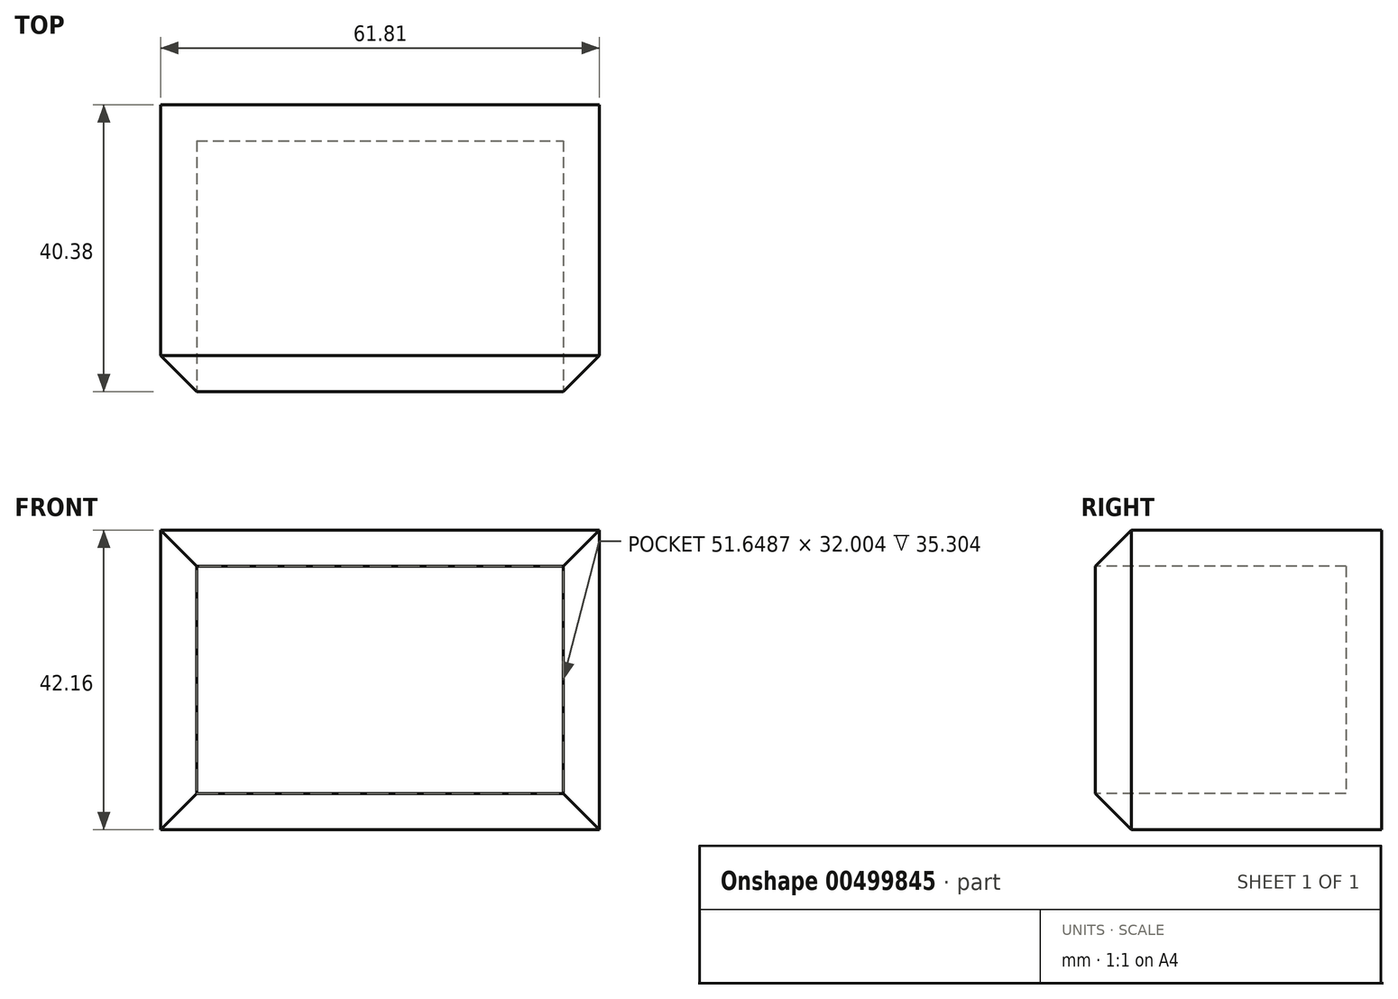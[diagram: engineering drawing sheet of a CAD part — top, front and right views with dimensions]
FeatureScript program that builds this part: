
annotation { "Feature Type Name" : "Feature", "Feature Type Description" : "" }
export const myFeature = defineFeature(function(context is Context, id is Id, definition is map)
    precondition{}
    {
        {
            var Q0;
            Q0=qCreatedBy(makeId("Top.planeOp"),FACE);
            var sketch = newSketch(context, id + "F0", { "sketchPlane" : qUnion([Q0])});
            skLineSegment(sketch, "E0.bottom", {"start": v(-33.75, 22.18) * mm, "end": v(28.06, 22.18) * mm});
            skLineSegment(sketch, "E0.top", {"start": v(-33.75, -18.2) * mm, "end": v(28.06, -18.2) * mm});
            skLineSegment(sketch, "E0.left", {"start": v(-33.75, 22.18) * mm, "end": v(-33.75, -18.2) * mm});
            skLineSegment(sketch, "E0.right", {"start": v(28.06, 22.18) * mm, "end": v(28.06, -18.2) * mm});
            skSolve(sketch);
        }
        {
            var Q0;
            Q0=makeQuery(id+"F0.imprint","IMPRINT",FACE,{"disambiguationData":[TD([[makeQuery(id+"F0.imprint","IMPRINT",EDGE,{"derivedFrom":sQuery(id+"F0.wireOp",EDGE,"E0.bottom")}),-1.0]])]});
            extrude(context, id + "F1", {"entities" : qUnion([Q0]), "depth" : 42.16 * mm});
        }
        {
            var Q0;
            Q0=makeQuery(id+"F1.opExtrude","SWEPT_FACE",FACE,{"disambiguationData":[OSD([sQuery(id+"F0.wireOp",EDGE,"E0.top")])]});
            shell(context, id + "F2", {"entities" : qUnion([Q0]), "thickness" : 5.08 * mm});
        }
        {
            var Q0;
            Q0=makeQuery(id+"F1.opExtrude","CAP_EDGE",EDGE,{"disambiguationData":[OSD([sQuery(id+"F0.wireOp",EDGE,"E0.top")])],"isStart":false});
            chamfer(context, id + "F3", {"entities" : qUnion([Q0]), "width" : 5.08 * mm, "tangentPropagation" : true});
        }
        {
            var Q0;
            Q0=makeQuery(id+"F1.opExtrude","SWEPT_EDGE",EDGE,{"disambiguationData":[OSD([sQuery(id+"F0.wireOp",EDGE,"E0.top"),sQuery(id+"F0.wireOp",EDGE,"E0.left")])]});
            var Q1;
            Q1=makeQuery(id+"F1.opExtrude","SWEPT_EDGE",EDGE,{"disambiguationData":[OSD([sQuery(id+"F0.wireOp",EDGE,"E0.top"),sQuery(id+"F0.wireOp",EDGE,"E0.right")])]});
            chamfer(context, id + "F4", {"entities" : qUnion([Q0, Q1]), "width" : 5.08 * mm, "tangentPropagation" : true});
        }
        {
            var Q0;
            Q0=makeQuery(id+"F1.opExtrude","CAP_EDGE",EDGE,{"disambiguationData":[OSD([sQuery(id+"F0.wireOp",EDGE,"E0.top")])],"isStart":true});
            chamfer(context, id + "F5", {"entities" : qUnion([Q0]), "width" : 5.08 * mm, "tangentPropagation" : true});
        }
    });
